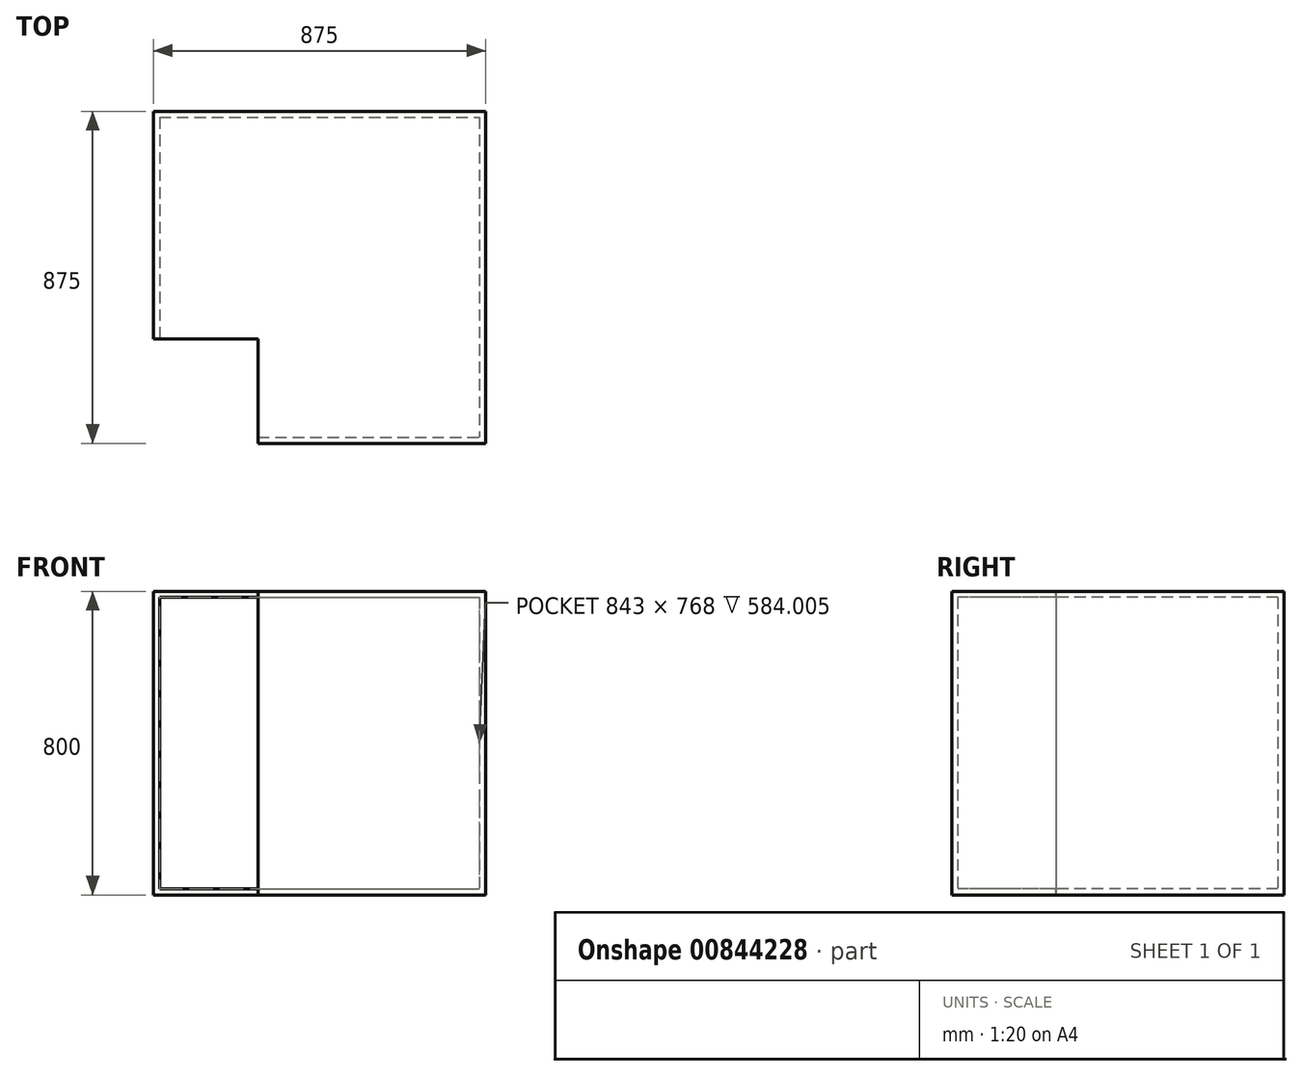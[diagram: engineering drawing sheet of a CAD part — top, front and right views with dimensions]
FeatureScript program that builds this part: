
annotation { "Feature Type Name" : "Feature", "Feature Type Description" : "" }
export const myFeature = defineFeature(function(context is Context, id is Id, definition is map)
    precondition{}
    {
        {
            var Q0;
            Q0=qCreatedBy(makeId("Top.planeOp"),FACE);
            var sketch = newSketch(context, id + "F0", { "sketchPlane" : qUnion([Q0])});
            skLineSegment(sketch, "E0.bottom", {"start": v(0, 0) * mm, "end": v(48.38, 0) * mm});
            skLineSegment(sketch, "E0.top", {"start": v(0, -50.25) * mm, "end": v(48.38, -50.25) * mm});
            skLineSegment(sketch, "E0.left", {"start": v(0, 0) * mm, "end": v(0, -50.25) * mm});
            skLineSegment(sketch, "E0.right", {"start": v(48.38, 0) * mm, "end": v(48.38, -50.25) * mm});
            skSolve(sketch);
        }
        {
            var Q0;
            Q0=makeQuery(id+"F0.imprint","IMPRINT",FACE,{"disambiguationData":[TD([[makeQuery(id+"F0.imprint","IMPRINT",EDGE,{"derivedFrom":sQuery(id+"F0.wireOp",EDGE,"E0.bottom")}),-1.0]])]});
            extrude(context, id + "F1", {"entities" : qUnion([Q0]), "depth" : 800 * mm, "offsetDistance" : 25 * mm});
        }
        {
            var Q0;
            Q0=makeQuery(id+"F1.opExtrude","SWEPT_FACE",FACE,{"disambiguationData":[OSD([sQuery(id+"F0.wireOp",EDGE,"E0.left")])]});
            extrude(context, id + "F2", {"entities" : qUnion([Q0]), "operationType" : NewBodyOperationType.ADD, "oppositeDirection" : true, "depth" : 875 * mm, "offsetDistance" : 25 * mm});
        }
        {
            var Q0;
            {var subQ0=sQuery(id+"F0.wireOp",EDGE,"E0.bottom");Q0=makeQuery(id+"F2.boolean.opBoolean","MERGE",FACE,{"derivedFrom":[makeQuery(id+"F1.opExtrude","SWEPT_FACE",FACE,{"disambiguationData":[OSD([subQ0])]}),makeQuery(id+"F2.opExtrude","SWEPT_FACE",FACE,{"disambiguationData":[OSD([subQ0,sQuery(id+"F0.wireOp",EDGE,"E0.left")])]})]});}
            extrude(context, id + "F3", {"entities" : qUnion([Q0]), "operationType" : NewBodyOperationType.ADD, "oppositeDirection" : true, "depth" : 875 * mm, "offsetDistance" : 25 * mm});
        }
        {
            var Q0;
            Q0=makeQuery(id+"F3.opExtrude","CAP_FACE",FACE,{"disambiguationData":[OSD([sQuery(id+"F0.wireOp",EDGE,"E0.bottom"),sQuery(id+"F0.wireOp",EDGE,"E0.left")])],"isStart":false});
            var sketch = newSketch(context, id + "F4", { "sketchPlane" : qUnion([Q0])});
            skLineSegment(sketch, "E1.bottom", {"start": v(875, 800) * mm, "end": v(344.03, 800) * mm});
            skLineSegment(sketch, "E1.top", {"start": v(875, 0) * mm, "end": v(344.03, 0) * mm});
            skLineSegment(sketch, "E1.left", {"start": v(875, 800) * mm, "end": v(875, 0) * mm});
            skLineSegment(sketch, "E1.right", {"start": v(344.03, 800) * mm, "end": v(344.03, 0) * mm});
            skSolve(sketch);
        }
        {
            var Q0;
            {var subQ0=sQuery(id+"F4.wireOp",EDGE,"E1.right");Q0=makeQuery(id+"F4.imprint","IMPRINT",FACE,{"disambiguationData":[TD([[makeQuery(id+"F4.imprint","IMPRINT",EDGE,{"derivedFrom":subQ0}),-1.0]])]});}
            extrude(context, id + "F5", {"entities" : qUnion([Q0]), "operationType" : NewBodyOperationType.REMOVE, "oppositeDirection" : true, "depth" : 100 * mm, "offsetDistance" : 25 * mm});
        }
        {
            var Q0;
            Q0=makeQuery(id+"F5.boolean.opBoolean","COPY",FACE,{"derivedFrom":makeQuery(id+"F5.opExtrude","SWEPT_FACE",FACE,{"disambiguationData":[OSD([sQuery(id+"F4.wireOp",EDGE,"E1.right")])]})});
            extrude(context, id + "F6", {"entities" : qUnion([Q0]), "operationType" : NewBodyOperationType.ADD, "depth" : 69.03 * mm, "offsetDistance" : 25 * mm});
        }
        {
            var Q0;
            {var subQ0=sQuery(id+"F0.wireOp",EDGE,"E0.left");var subQ1=sQuery(id+"F0.wireOp",EDGE,"E0.bottom");Q0=makeQuery(id+"F3.boolean.opBoolean","MERGE",FACE,{"derivedFrom":[makeQuery(id+"F1.opExtrude","SWEPT_FACE",FACE,{"disambiguationData":[OSD([subQ0])]}),makeQuery(id+"F3.opExtrude","SWEPT_FACE",FACE,{"disambiguationData":[OSD([subQ1,subQ0]),TDD([makeQuery(id+"F1.opExtrude","SWEPT_EDGE",EDGE,{"disambiguationData":[OSD([subQ1,subQ0])]})])]})]});}
            var sketch = newSketch(context, id + "F7", { "sketchPlane" : qUnion([Q0])});
            skLineSegment(sketch, "E2.bottom", {"start": v(0, 800) * mm, "end": v(519.51, 800) * mm});
            skLineSegment(sketch, "E2.top", {"start": v(0, 0) * mm, "end": v(519.51, 0) * mm});
            skLineSegment(sketch, "E2.left", {"start": v(0, 800) * mm, "end": v(0, 0) * mm});
            skLineSegment(sketch, "E2.right", {"start": v(519.51, 800) * mm, "end": v(519.51, 0) * mm});
            skSolve(sketch);
        }
        {
            var Q0;
            {var subQ0=sQuery(id+"F7.wireOp",EDGE,"E2.right");Q0=makeQuery(id+"F7.imprint","IMPRINT",FACE,{"disambiguationData":[TD([[makeQuery(id+"F7.imprint","IMPRINT",EDGE,{"derivedFrom":subQ0}),1.0]])]});}
            extrude(context, id + "F8", {"entities" : qUnion([Q0]), "operationType" : NewBodyOperationType.REMOVE, "oppositeDirection" : true, "depth" : 100 * mm, "offsetDistance" : 25 * mm});
        }
        {
            var Q0;
            Q0=makeQuery(id+"F8.boolean.opBoolean","COPY",FACE,{"derivedFrom":makeQuery(id+"F8.opExtrude","SWEPT_FACE",FACE,{"disambiguationData":[OSD([sQuery(id+"F7.wireOp",EDGE,"E2.right")])]})});
            extrude(context, id + "F9", {"entities" : qUnion([Q0]), "operationType" : NewBodyOperationType.ADD, "depth" : 80.49 * mm, "offsetDistance" : 25 * mm});
        }
        {
            var Q0;
            Q0=makeQuery(id+"F5.boolean.opBoolean","COPY",FACE,{"derivedFrom":makeQuery(id+"F5.opExtrude","CAP_FACE",FACE,{"disambiguationData":[OSD([sQuery(id+"F0.wireOp",EDGE,"E0.bottom"),sQuery(id+"F0.wireOp",EDGE,"E0.left"),sQuery(id+"F4.wireOp",EDGE,"E1.right")])],"isStart":false})});
            extrude(context, id + "F10", {"entities" : qUnion([Q0]), "operationType" : NewBodyOperationType.REMOVE, "oppositeDirection" : true, "depth" : 175 * mm, "offsetDistance" : 25 * mm});
        }
        {
            var Q0;
            {var subQ0=sQuery(id+"F4.wireOp",EDGE,"E1.right");Q0=makeQuery(id+"F10.boolean.opBoolean","MERGE",FACE,{"derivedFrom":[makeQuery(id+"F6.opExtrude","CAP_FACE",FACE,{"disambiguationData":[OSD([subQ0])],"isStart":false}),makeQuery(id+"F10.opExtrude","SWEPT_FACE",FACE,{"disambiguationData":[OSD([subQ0])]})]});}
            shell(context, id + "F11", {"entities" : qUnion([Q0]), "thickness" : 16 * mm});
        }
        {
            var Q0;
            Q0=makeQuery(id+"F10.boolean.opBoolean","COPY",FACE,{"derivedFrom":makeQuery(id+"F10.opExtrude","CAP_FACE",FACE,{"disambiguationData":[OSD([sQuery(id+"F0.wireOp",EDGE,"E0.bottom"),sQuery(id+"F0.wireOp",EDGE,"E0.left"),sQuery(id+"F4.wireOp",EDGE,"E1.right")])],"isStart":false})});
            extrude(context, id + "F12", {"entities" : qUnion([Q0]), "operationType" : NewBodyOperationType.REMOVE, "oppositeDirection" : true, "depth" : 16 * mm, "offsetDistance" : 25 * mm});
        }
        {
            var Q0;
            Q0=makeQuery(id+"F9.opExtrude","CAP_FACE",FACE,{"disambiguationData":[OSD([sQuery(id+"F7.wireOp",EDGE,"E2.right")])],"isStart":false});
            extrude(context, id + "F13", {"entities" : qUnion([Q0]), "operationType" : NewBodyOperationType.REMOVE, "oppositeDirection" : true, "depth" : 16 * mm, "offsetDistance" : 25 * mm});
        }
        {
            var Q0;
            Q0=makeQuery(id+"F13.boolean.opBoolean","COPY",FACE,{"derivedFrom":makeQuery(id+"F13.opExtrude","CAP_FACE",FACE,{"disambiguationData":[OSD([sQuery(id+"F7.wireOp",EDGE,"E2.right")])],"isStart":false})});
            var Q1;
            {var subQ1=sQuery(id+"F4.wireOp",EDGE,"E1.right");var subQ3=sQuery(id+"F0.wireOp",EDGE,"E0.left");var subQ4=sQuery(id+"F0.wireOp",EDGE,"E0.bottom");Q1=makeQuery(id+"F12.boolean.opBoolean","COPY",FACE,{"disambiguationData":[TD([makeQuery(id+"F2.opExtrude","SWEPT_FACE",FACE,{"disambiguationData":[OSD([subQ3]),TDD([makeQuery(id+"F1.opExtrude","CAP_EDGE",EDGE,{"disambiguationData":[OSD([subQ3])],"isStart":true})])]})])],"derivedFrom":makeQuery(id+"F12.opExtrude","CAP_FACE",FACE,{"disambiguationData":[OSD([subQ4,subQ3,subQ1])],"isStart":false})});}
            var Q2;
            {var subQ2=sQuery(id+"F0.wireOp",EDGE,"E0.left");var subQ3=sQuery(id+"F0.wireOp",EDGE,"E0.bottom");var subQ4=sQuery(id+"F4.wireOp",EDGE,"E1.right");Q2=makeQuery(id+"F12.boolean.opBoolean","COPY",FACE,{"disambiguationData":[TD([makeQuery(id+"F2.opExtrude","SWEPT_FACE",FACE,{"disambiguationData":[OSD([subQ2]),TDD([makeQuery(id+"F1.opExtrude","CAP_EDGE",EDGE,{"disambiguationData":[OSD([subQ2])],"isStart":false})])]})])],"derivedFrom":makeQuery(id+"F12.opExtrude","CAP_FACE",FACE,{"disambiguationData":[OSD([subQ3,subQ2,subQ4])],"isStart":false})});}
            extrude(context, id + "F14", {"entities" : qUnion([Q0, Q1, Q2]), "operationType" : NewBodyOperationType.ADD, "depth" : 16 * mm, "offsetDistance" : 25 * mm});
        }
    });
